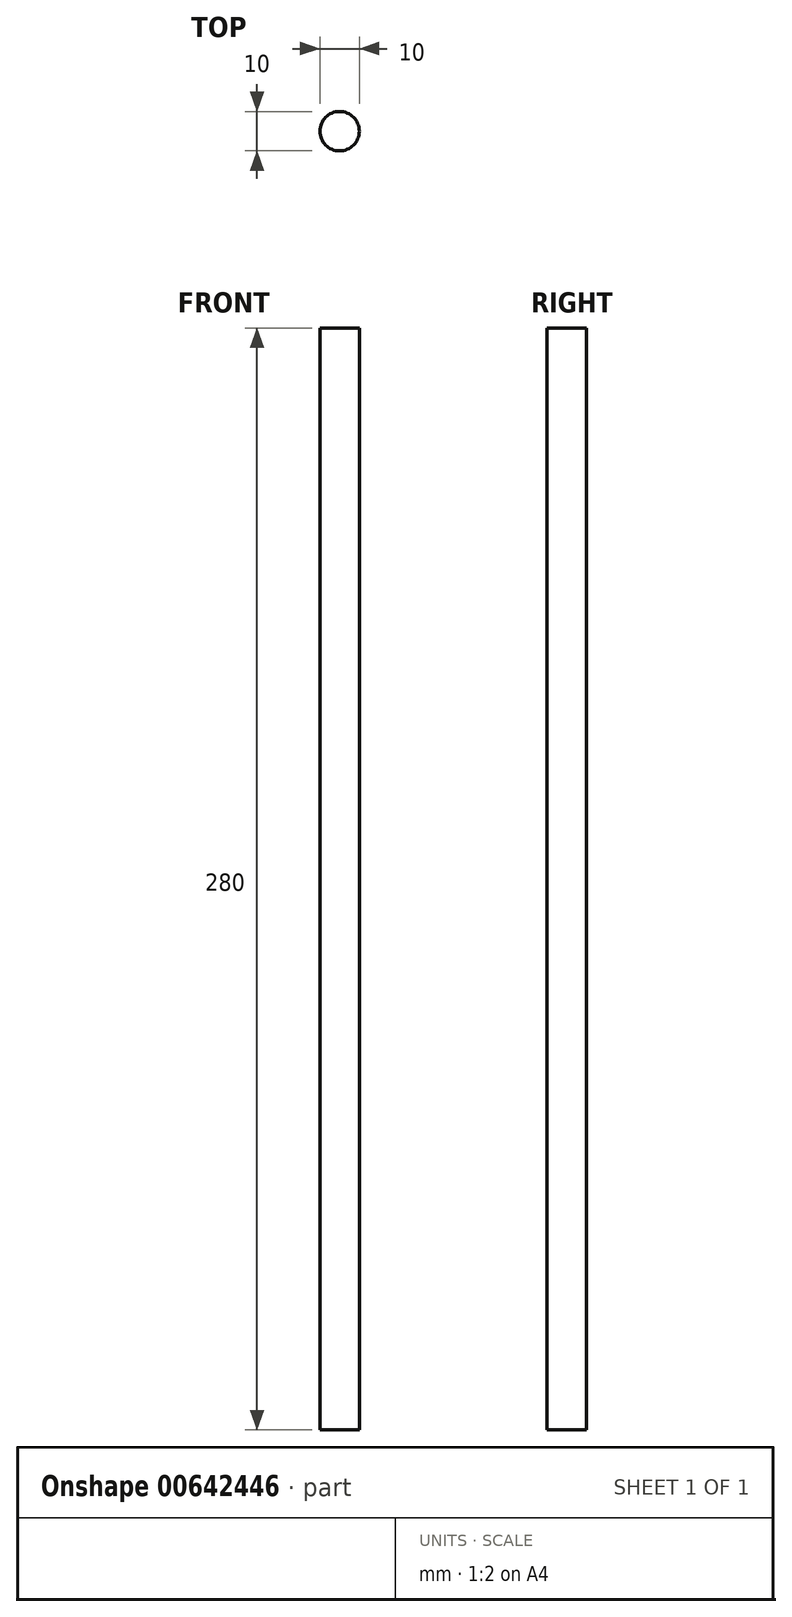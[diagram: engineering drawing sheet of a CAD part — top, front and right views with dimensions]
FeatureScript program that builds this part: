
annotation { "Feature Type Name" : "Feature", "Feature Type Description" : "" }
export const myFeature = defineFeature(function(context is Context, id is Id, definition is map)
    precondition{}
    {
        {
            var Q0;
            Q0=qCreatedBy(makeId("Top.planeOp"),FACE);
            var sketch = newSketch(context, id + "F0", { "sketchPlane" : qUnion([Q0])});
            skCircle(sketch, "E0", {"center": v(0, 0) * mm, "radius": 5 * mm});
            skSolve(sketch);
        }
        {
            var Q0;
            Q0=makeQuery(id+"F0.imprint","IMPRINT",FACE,{"disambiguationData":[TD([[makeQuery(id+"F0.imprint","IMPRINT",EDGE,{"derivedFrom":sQuery(id+"F0.wireOp",EDGE,"E0")}),1.0]])]});
            extrude(context, id + "F1", {"entities" : qUnion([Q0]), "depth" : 280 * mm, "offsetDistance" : 25 * mm});
        }
    });
